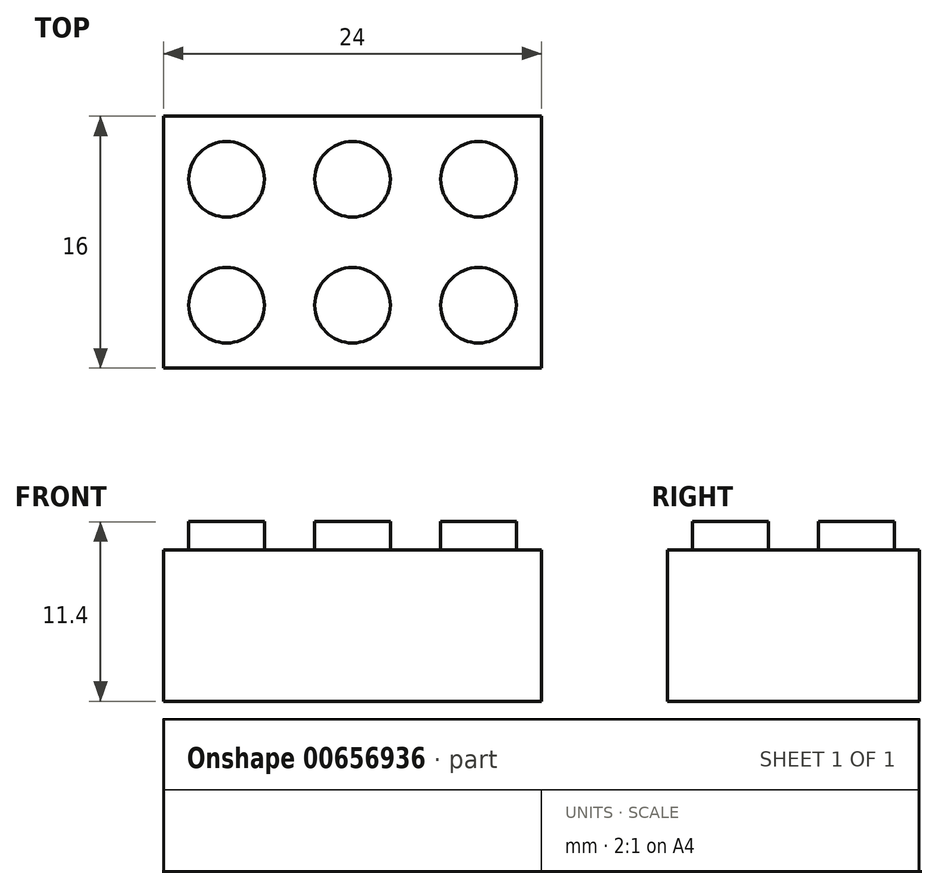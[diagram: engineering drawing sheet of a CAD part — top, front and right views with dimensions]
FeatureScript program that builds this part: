
annotation { "Feature Type Name" : "Feature", "Feature Type Description" : "" }
export const myFeature = defineFeature(function(context is Context, id is Id, definition is map)
    precondition{}
    {
        {
            var Q0;
            Q0=qCreatedBy(makeId("Top.planeOp"),FACE);
            var sketch = newSketch(context, id + "F0", { "sketchPlane" : qUnion([Q0])});
            skLineSegment(sketch, "E0.bottom", {"start": v(0, 0) * mm, "end": v(-24, 0) * mm});
            skLineSegment(sketch, "E0.top", {"start": v(0, 16) * mm, "end": v(-24, 16) * mm});
            skLineSegment(sketch, "E0.left", {"start": v(0, 0) * mm, "end": v(0, 16) * mm});
            skLineSegment(sketch, "E0.right", {"start": v(-24, 0) * mm, "end": v(-24, 16) * mm});
            skSolve(sketch);
        }
        {
            var Q0;
            Q0=makeQuery(id+"F0.imprint","IMPRINT",FACE,{"disambiguationData":[TD([[makeQuery(id+"F0.imprint","IMPRINT",EDGE,{"derivedFrom":sQuery(id+"F0.wireOp",EDGE,"E0.bottom")}),-1.0]])]});
            extrude(context, id + "F1", {"entities" : qUnion([Q0]), "depth" : 9.6 * mm, "offsetDistance" : 25.4 * mm});
        }
        {
            var Q0;
            Q0=makeQuery(id+"F1.opExtrude","CAP_FACE",FACE,{"disambiguationData":[OSD([sQuery(id+"F0.wireOp",EDGE,"E0.bottom"),sQuery(id+"F0.wireOp",EDGE,"E0.top"),sQuery(id+"F0.wireOp",EDGE,"E0.left"),sQuery(id+"F0.wireOp",EDGE,"E0.right")])],"isStart":false});
            var sketch = newSketch(context, id + "F2", { "sketchPlane" : qUnion([Q0])});
            skLineSegment(sketch, "E1", {"start": v(-24, 8) * mm, "end": v(0, 8) * mm});
            skLineSegment(sketch, "E2", {"start": v(-16, 16) * mm, "end": v(-16, 0) * mm});
            skLineSegment(sketch, "E3", {"start": v(-8, 16) * mm, "end": v(-8, 0) * mm});
            skLineSegment(sketch, "E4", {"start": v(-24, 16) * mm, "end": v(-16, 8) * mm, "construction": true});
            skLineSegment(sketch, "E5", {"start": v(-16, 8) * mm, "end": v(-8, 16) * mm, "construction": true});
            skLineSegment(sketch, "E6", {"start": v(-8, 16) * mm, "end": v(0, 8) * mm, "construction": true});
            skCircle(sketch, "E7", {"center": v(-20, 12) * mm, "radius": 2.4 * mm});
            skCircle(sketch, "E8", {"center": v(-12, 12) * mm, "radius": 2.4 * mm});
            skCircle(sketch, "E9", {"center": v(-4, 12) * mm, "radius": 2.4 * mm});
            skCircle(sketch, "E10.MirrorC", {"center": v(-20, 4) * mm, "radius": 2.4 * mm});
            skCircle(sketch, "E11.MirrorC", {"center": v(-12, 4) * mm, "radius": 2.4 * mm});
            skCircle(sketch, "E12.MirrorC", {"center": v(-4, 4) * mm, "radius": 2.4 * mm});
            skSolve(sketch);
        }
        {
            var Q0;
            Q0 = qSketchRegion(id + "F2", true);
            extrude(context, id + "F3", {"entities" : qUnion([Q0]), "operationType" : NewBodyOperationType.ADD, "depth" : 1.8 * mm, "offsetDistance" : 25.4 * mm});
        }
    });
